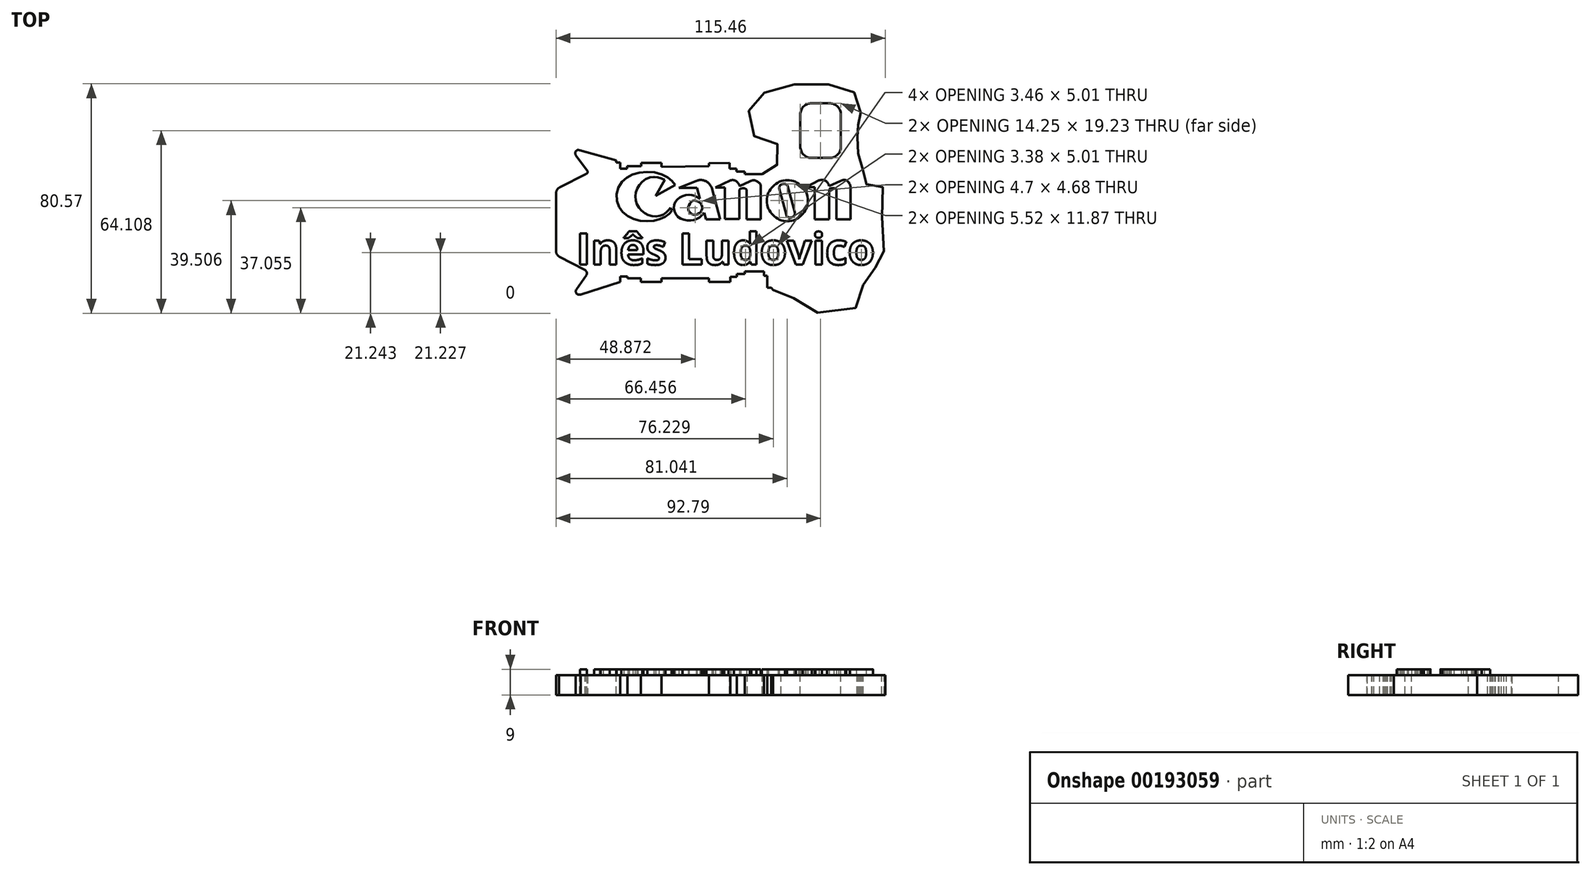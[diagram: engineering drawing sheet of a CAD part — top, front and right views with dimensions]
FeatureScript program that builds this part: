
annotation { "Feature Type Name" : "Feature", "Feature Type Description" : "" }
export const myFeature = defineFeature(function(context is Context, id is Id, definition is map)
    precondition{}
    {
        {
            var Q0;
            Q0=qCreatedBy(makeId("Top.planeOp"),FACE);
            var sketch = newSketch(context, id + "F0", { "sketchPlane" : qUnion([Q0])});
            skLineSegment(sketch, "E0", {"start": v(25.55, 22.7) * mm, "end": v(22.34, 17.11) * mm});
            skLineSegment(sketch, "E1", {"start": v(22.34, 17.11) * mm, "end": v(29.25, 20.87) * mm});
            skLineSegment(sketch, "E2", {"start": v(27.55, 12.91) * mm, "end": v(28.1, 11.89) * mm});
            skLineSegment(sketch, "E3", {"start": v(36.86, 19.9) * mm, "end": v(30.53, 19.9) * mm});
            skLineSegment(sketch, "E4", {"start": v(30.53, 19.9) * mm, "end": v(36.65, 22.37) * mm});
            skLineSegment(sketch, "E5", {"start": v(36.86, 19.9) * mm, "end": v(37.86, 16.15) * mm});
            skLineSegment(sketch, "E6", {"start": v(39.39, 11.08) * mm, "end": v(39.97, 8.89) * mm});
            skLineSegment(sketch, "E7", {"start": v(39.97, 8.89) * mm, "end": v(44.97, 8.89) * mm});
            skLineSegment(sketch, "E8", {"start": v(44.97, 8.89) * mm, "end": v(42.04, 19.9) * mm});
            skLineSegment(sketch, "E9", {"start": v(48.66, 22.57) * mm, "end": v(43.34, 20.06) * mm});
            skLineSegment(sketch, "E10", {"start": v(43.34, 20.06) * mm, "end": v(46.62, 20.06) * mm});
            skLineSegment(sketch, "E11", {"start": v(46.62, 20.06) * mm, "end": v(46.62, 8.93) * mm});
            skLineSegment(sketch, "E12", {"start": v(46.62, 8.93) * mm, "end": v(51.76, 8.93) * mm});
            skLineSegment(sketch, "E13", {"start": v(51.76, 8.93) * mm, "end": v(51.76, 19.12) * mm});
            skLineSegment(sketch, "E14", {"start": v(54.28, 19.05) * mm, "end": v(54.28, 8.84) * mm});
            skLineSegment(sketch, "E15", {"start": v(54.28, 8.84) * mm, "end": v(59.22, 8.84) * mm});
            skLineSegment(sketch, "E16", {"start": v(59.22, 8.84) * mm, "end": v(59.22, 20.47) * mm});
            skLineSegment(sketch, "E17", {"start": v(51.83, 20.55) * mm, "end": v(55.42, 22.2) * mm});
            skCircle(sketch, "E18", {"center": v(68.54, 15.4) * mm, "radius": 7.18 * mm});
            skLineSegment(sketch, "E19", {"start": v(65.68, 19.69) * mm, "end": v(68.18, 10.33) * mm});
            skLineSegment(sketch, "E20", {"start": v(68.64, 20.6) * mm, "end": v(71.14, 11.46) * mm});
            skLineSegment(sketch, "E21", {"start": v(79.7, 22.51) * mm, "end": v(75.06, 20.1) * mm});
            skLineSegment(sketch, "E22", {"start": v(75.06, 20.1) * mm, "end": v(78.1, 20.1) * mm});
            skLineSegment(sketch, "E23", {"start": v(78.1, 20.1) * mm, "end": v(78.1, 8.88) * mm});
            skLineSegment(sketch, "E24", {"start": v(78.1, 8.88) * mm, "end": v(83.2, 8.88) * mm});
            skLineSegment(sketch, "E25", {"start": v(83.2, 8.88) * mm, "end": v(83.2, 19.16) * mm});
            skLineSegment(sketch, "E26", {"start": v(85.75, 19) * mm, "end": v(85.75, 8.9) * mm});
            skLineSegment(sketch, "E27", {"start": v(85.75, 8.9) * mm, "end": v(90.69, 8.9) * mm});
            skLineSegment(sketch, "E28", {"start": v(90.69, 8.9) * mm, "end": v(90.69, 20.51) * mm});
            skLineSegment(sketch, "E29", {"start": v(83.21, 20.55) * mm, "end": v(87.16, 22.36) * mm});
            skFitSpline(sketch, "E30", {"points": [v(87.16, 22.36) * mm, v(88.44, 22.69) * mm, v(89.84, 22.08) * mm, v(90.69, 20.51) * mm], "startDerivative": vector(4.02, 1.64) * mm, "endDerivative": vector(1.85, -4.85) * mm});
            skFitSpline(sketch, "E31", {"points": [v(79.7, 22.51) * mm, v(80.8, 22.69) * mm, v(82.34, 22.06) * mm, v(83.21, 20.55) * mm], "startDerivative": vector(3.56, 1.05) * mm, "endDerivative": vector(1.86, -4.65) * mm});
            skFitSpline(sketch, "E32", {"points": [v(83.2, 19.16) * mm, v(84, 19.77) * mm, v(85.05, 19.78) * mm, v(85.75, 19) * mm], "startDerivative": vector(1.8, 4.83) * mm, "endDerivative": vector(0.96, -4.57) * mm});
            skFitSpline(sketch, "E33", {"points": [v(65.68, 19.69) * mm, v(66, 20.79) * mm, v(67.73, 21.3) * mm, v(68.64, 20.6) * mm], "startDerivative": vector(0.1, 3.88) * mm, "endDerivative": vector(2.36, -3) * mm});
            skFitSpline(sketch, "E34", {"points": [v(71.14, 11.46) * mm, v(70.7, 9.89) * mm, v(69.36, 9.46) * mm, v(68.18, 10.33) * mm], "startDerivative": vector(1.8, -7.45) * mm, "endDerivative": vector(-2.16, 5.47) * mm});
            skFitSpline(sketch, "E35", {"points": [v(55.42, 22.2) * mm, v(56.74, 22.57) * mm, v(58.26, 21.97) * mm, v(59.22, 20.47) * mm], "startDerivative": vector(4.12, 1.85) * mm, "endDerivative": vector(0.6, -6.79) * mm});
            skFitSpline(sketch, "E36", {"points": [v(51.76, 19.12) * mm, v(52.53, 19.72) * mm, v(53.4, 19.74) * mm, v(54.28, 19.05) * mm], "startDerivative": vector(0.57, 3.43) * mm, "endDerivative": vector(1.8, -4.71) * mm});
            skFitSpline(sketch, "E37", {"points": [v(48.66, 22.57) * mm, v(49.98, 22.57) * mm, v(51.2, 21.7) * mm, v(51.83, 20.55) * mm], "startDerivative": vector(4.07, 0.59) * mm, "endDerivative": vector(1.6, -3.62) * mm});
            skFitSpline(sketch, "E38", {"points": [v(36.65, 22.37) * mm, v(38.17, 22.68) * mm, v(39.66, 22.37) * mm, v(41.07, 21.46) * mm, v(42.04, 19.9) * mm], "startDerivative": vector(6.26, 1.9) * mm, "endDerivative": vector(3.2, -6.44) * mm});
            skFitSpline(sketch, "E39", {"points": [v(37.86, 16.15) * mm, v(35.45, 17.27) * mm, v(32.42, 17.24) * mm, v(29.68, 15.5) * mm, v(28.77, 12.57) * mm, v(30.3, 9.6) * mm, v(33.67, 8.48) * mm, v(36.81, 8.95) * mm, v(39.39, 11.08) * mm], "startDerivative": vector(-20.05, 11.67) * mm, "endDerivative": vector(18.93, 19.47) * mm});
            skFitSpline(sketch, "E40", {"points": [v(35.36, 15.28) * mm, v(34.05, 13.9) * mm, v(33.97, 11.85) * mm, v(35.58, 10.54) * mm, v(37.73, 11.06) * mm, v(38.7, 12.83) * mm, v(38.02, 14.6) * mm, v(36.69, 15.3) * mm, v(35.36, 15.28) * mm]});
            skFitSpline(sketch, "E41", {"points": [v(25.55, 22.7) * mm, v(22.92, 23.67) * mm, v(19.35, 23.24) * mm, v(16.4, 20.56) * mm, v(15.28, 17.49) * mm, v(15.73, 14.19) * mm, v(17.82, 11.56) * mm, v(20.57, 10.14) * mm, v(23.96, 10.1) * mm, v(26.14, 11.31) * mm, v(27.55, 12.91) * mm], "startDerivative": vector(-26.12, 12.48) * mm, "endDerivative": vector(15.76, 20.13) * mm});
            skFitSpline(sketch, "E42", {"points": [v(29.25, 20.87) * mm, v(27.38, 22.95) * mm, v(23.88, 24.86) * mm, v(18.1, 25.5) * mm, v(13.3, 24.13) * mm, v(10.2, 21.61) * mm, v(8.67, 17.42) * mm, v(9.54, 13.21) * mm, v(12.16, 10.3) * mm, v(16.04, 8.58) * mm, v(20.51, 8.24) * mm, v(24.56, 9.21) * mm, v(26.81, 10.52) * mm, v(28.1, 11.89) * mm], "startDerivative": vector(-25.89, 32.96) * mm, "endDerivative": vector(22.29, 26.43) * mm});
            skSolve(sketch);
        }
        {
            var Q0;
            Q0=makeQuery(id+"F0.imprint","IMPRINT",FACE,{"disambiguationData":[TD([[makeQuery(id+"F0.imprint","IMPRINT",EDGE,{"derivedFrom":sQuery(id+"F0.wireOp",EDGE,"E21")}),1.0]])]});
            var Q1;
            Q1=makeQuery(id+"F0.imprint","IMPRINT",FACE,{"disambiguationData":[TD([[makeQuery(id+"F0.imprint","IMPRINT",EDGE,{"derivedFrom":sQuery(id+"F0.wireOp",EDGE,"E18")}),1.0]])]});
            var Q2;
            Q2=makeQuery(id+"F0.imprint","IMPRINT",FACE,{"disambiguationData":[TD([[makeQuery(id+"F0.imprint","IMPRINT",EDGE,{"derivedFrom":sQuery(id+"F0.wireOp",EDGE,"E9")}),1.0]])]});
            var Q3;
            Q3=makeQuery(id+"F0.imprint","IMPRINT",FACE,{"disambiguationData":[TD([[makeQuery(id+"F0.imprint","IMPRINT",EDGE,{"derivedFrom":sQuery(id+"F0.wireOp",EDGE,"E3")}),-1.0]])]});
            var Q4;
            Q4=makeQuery(id+"F0.imprint","IMPRINT",FACE,{"disambiguationData":[TD([[makeQuery(id+"F0.imprint","IMPRINT",EDGE,{"derivedFrom":sQuery(id+"F0.wireOp",EDGE,"E0")}),1.0]])]});
            extrude(context, id + "F1", {"entities" : qUnion([Q0, Q1, Q2, Q3, Q4]), "depth" : 2 * mm});
        }
        {
            var Q0;
            Q0=qCreatedBy(makeId("Top.planeOp"),FACE);
            var sketch = newSketch(context, id + "F2", { "sketchPlane" : qUnion([Q0])});
            skText(sketch, "E43", { "text": "Inês Ludovico", "fontName": "OpenSans-Bold.ttf"});
            const initialGuessF2  = {"E43": [-0.0055, -0.00706, 1, 0, 0.01106]};
            skSetInitialGuess(sketch, initialGuessF2);
            skSolve(sketch);
        }
        {
            var Q0;
            Q0=qSketchRegion(id+"F2",true);
            extrude(context, id + "F3", {"entities" : qUnion([Q0]), "depth" : 2 * mm});
        }
        {
            var Q0;
            Q0=qCreatedBy(makeId("Top.planeOp"),FACE);
            var sketch = newSketch(context, id + "F4", { "sketchPlane" : qUnion([Q0])});
            skLineSegment(sketch, "E44", {"start": v(-4.27, 33.12) * mm, "end": v(8.5, 29.54) * mm});
            skLineSegment(sketch, "E45", {"start": v(8.5, 29.54) * mm, "end": v(8.5, 28.85) * mm});
            skLineSegment(sketch, "E46", {"start": v(8.5, 28.85) * mm, "end": v(9.98, 28.85) * mm});
            skLineSegment(sketch, "E47", {"start": v(9.98, 28.85) * mm, "end": v(9.98, 26.64) * mm});
            skLineSegment(sketch, "E48", {"start": v(9.98, 26.64) * mm, "end": v(12.34, 26.64) * mm});
            skLineSegment(sketch, "E49", {"start": v(12.34, 26.64) * mm, "end": v(12.34, 27.52) * mm});
            skLineSegment(sketch, "E50", {"start": v(12.34, 27.52) * mm, "end": v(17.25, 27.52) * mm});
            skLineSegment(sketch, "E51", {"start": v(17.25, 27.52) * mm, "end": v(17.25, 28.65) * mm});
            skLineSegment(sketch, "E52", {"start": v(17.25, 28.65) * mm, "end": v(24.43, 28.65) * mm});
            skLineSegment(sketch, "E53", {"start": v(24.43, 28.65) * mm, "end": v(24.43, 27.32) * mm});
            skLineSegment(sketch, "E54", {"start": v(24.43, 27.32) * mm, "end": v(41.08, 27.52) * mm});
            skPoint(sketch, "E54.endSnap0", {"position": v(14.8, 27.52) * mm});
            skLineSegment(sketch, "E55", {"start": v(41.08, 27.52) * mm, "end": v(41.07, 28.58) * mm});
            skLineSegment(sketch, "E56", {"start": v(41.07, 28.58) * mm, "end": v(48.22, 28.66) * mm});
            skLineSegment(sketch, "E57", {"start": v(48.22, 28.66) * mm, "end": v(48.25, 26.59) * mm});
            skLineSegment(sketch, "E58", {"start": v(48.25, 26.59) * mm, "end": v(50.73, 26.62) * mm});
            skLineSegment(sketch, "E59", {"start": v(50.73, 26.62) * mm, "end": v(50.74, 25.63) * mm});
            skLineSegment(sketch, "E60", {"start": v(50.74, 25.63) * mm, "end": v(53.6, 25.67) * mm});
            skLineSegment(sketch, "E61", {"start": v(53.6, 25.67) * mm, "end": v(53.6, 24.68) * mm});
            skLineSegment(sketch, "E62", {"start": v(53.6, 24.68) * mm, "end": v(59.69, 24.75) * mm});
            skFitSpline(sketch, "E63", {"points": [v(59.69, 24.75) * mm, v(60.26, 25.63) * mm, v(61.5, 26.44) * mm, v(62.74, 26.5) * mm, v(64.36, 27.37) * mm, v(65.59, 29) * mm, v(66.18, 31.16) * mm, v(66.23, 33.61) * mm, v(64.95, 35.33) * mm, v(62.98, 35.97) * mm, v(60.03, 36.37) * mm, v(57.33, 37.74) * mm, v(55.6, 39.48) * mm, v(54.53, 42.7) * mm, v(54.86, 46.33) * mm, v(55.75, 48.71) * mm, v(57.24, 50.7) * mm, v(59.17, 52.42) * mm, v(62.3, 54.24) * mm, v(66.1, 55.5) * mm, v(70.88, 56.17) * mm, v(76.66, 56.43) * mm, v(81.08, 56.38) * mm, v(85.82, 55.8) * mm, v(88.74, 55.18) * mm, v(91.03, 54.2) * mm, v(93.06, 51.8) * mm, v(93.84, 48.78) * mm, v(94, 47.13) * mm, v(94.05, 46.53) * mm, v(94.4, 46) * mm, v(94.47, 45.25) * mm, v(94.34, 44.1) * mm, v(93.9, 43.61) * mm, v(93.6, 43.28) * mm, v(93.5, 42.65) * mm, v(93.38, 41.84) * mm, v(93.53, 41.35) * mm, v(93.98, 40.92) * mm, v(94.23, 39.46) * mm, v(93.8, 38.5) * mm, v(93.3, 37.98) * mm, v(93.02, 37.4) * mm, v(93.06, 35.8) * mm, v(93.1, 33.97) * mm, v(93.1, 32.7) * mm, v(93.1, 32.15) * mm, v(93.42, 31.82) * mm, v(93.75, 31.22) * mm, v(93.84, 30.06) * mm, v(94.53, 29.32) * mm, v(95.04, 27.79) * mm, v(95, 25.6) * mm, v(94.77, 24.75) * mm, v(94.81, 23.92) * mm, v(95.6, 23) * mm, v(96.13, 22.21) * mm, v(96.35, 21.07) * mm, v(96.91, 21.07) * mm, v(98.27, 21.07) * mm, v(99.67, 21.07) * mm, v(101.12, 20.77) * mm, v(102.43, 19.28) * mm, v(102.22, 15.3) * mm, v(101.8, 10.84) * mm, v(101.68, 5.8) * mm, v(102, 0) * mm, v(102.58, -3.28) * mm, v(102.84, -5.38) * mm, v(101.88, -7.4) * mm, v(99.78, -8.18) * mm, v(97.24, -8.27) * mm, v(96.2, -10.19) * mm, v(95.5, -12.83) * mm, v(94.8, -15.64) * mm, v(94.46, -18.3) * mm, v(94, -20.63) * mm, v(91.03, -23.04) * mm, v(83.93, -24.1) * mm, v(77.9, -23.72) * mm, v(73.63, -22.18) * mm, v(71.42, -19.97) * mm, v(70.31, -18.2) * mm, v(68.55, -16.58) * mm, v(65.38, -15.92) * mm, v(63.47, -15.92) * mm], "startDerivative": vector(54.76, 104.15) * mm, "endDerivative": vector(-153.88, -5.36) * mm});
            skLineSegment(sketch, "E64", {"start": v(63.47, -15.92) * mm, "end": v(62.9, -15.16) * mm});
            skLineSegment(sketch, "E65", {"start": v(62.9, -15.16) * mm, "end": v(61.49, -15.16) * mm});
            skLineSegment(sketch, "E66", {"start": v(61.49, -15.16) * mm, "end": v(61.49, -11) * mm});
            skLineSegment(sketch, "E67", {"start": v(61.49, -11) * mm, "end": v(60.4, -11) * mm});
            skLineSegment(sketch, "E68", {"start": v(60.4, -11) * mm, "end": v(60.4, -9.49) * mm});
            skLineSegment(sketch, "E69", {"start": v(60.4, -9.49) * mm, "end": v(53.68, -9.49) * mm});
            skLineSegment(sketch, "E70", {"start": v(53.68, -9.49) * mm, "end": v(53.68, -10.27) * mm});
            skLineSegment(sketch, "E71", {"start": v(53.68, -10.27) * mm, "end": v(50.81, -10.27) * mm});
            skLineSegment(sketch, "E72", {"start": v(50.81, -10.27) * mm, "end": v(50.81, -11.3) * mm});
            skLineSegment(sketch, "E73", {"start": v(50.81, -11.3) * mm, "end": v(48.58, -11.3) * mm});
            skLineSegment(sketch, "E74", {"start": v(48.58, -11.3) * mm, "end": v(48.58, -13.08) * mm});
            skLineSegment(sketch, "E75", {"start": v(48.58, -13.08) * mm, "end": v(41.03, -13.08) * mm});
            skLineSegment(sketch, "E76", {"start": v(41.03, -13.08) * mm, "end": v(41.03, -11.83) * mm});
            skLineSegment(sketch, "E77", {"start": v(41.03, -11.83) * mm, "end": v(24.46, -11.83) * mm});
            skLineSegment(sketch, "E78", {"start": v(24.46, -11.83) * mm, "end": v(24.46, -13.08) * mm});
            skLineSegment(sketch, "E79", {"start": v(24.46, -13.08) * mm, "end": v(17.18, -13.08) * mm});
            skLineSegment(sketch, "E80", {"start": v(17.18, -13.08) * mm, "end": v(17.18, -11.83) * mm});
            skLineSegment(sketch, "E81", {"start": v(17.18, -11.83) * mm, "end": v(12.49, -11.83) * mm});
            skLineSegment(sketch, "E82", {"start": v(12.49, -11.83) * mm, "end": v(12.49, -11.25) * mm});
            skLineSegment(sketch, "E83", {"start": v(12.49, -11.25) * mm, "end": v(9.98, -11.25) * mm});
            skLineSegment(sketch, "E84", {"start": v(9.98, -11.25) * mm, "end": v(9.98, -13.08) * mm});
            skLineSegment(sketch, "E85", {"start": v(9.98, -13.08) * mm, "end": v(-3.92, -17.55) * mm});
            skLineSegment(sketch, "E86", {"start": v(-5.45, -15.73) * mm, "end": v(-1.92, -10.72) * mm});
            skLineSegment(sketch, "E87", {"start": v(-2.35, -8.98) * mm, "end": v(-11.49, -4.22) * mm});
            skLineSegment(sketch, "E88", {"start": v(-12.6, 17.98) * mm, "end": v(-12.6, -1.95) * mm});
            skLineSegment(sketch, "E89", {"start": v(-11.1, 20.15) * mm, "end": v(-2.07, 24.7) * mm});
            skLineSegment(sketch, "E90", {"start": v(-1.76, 26.16) * mm, "end": v(-5.65, 31.3) * mm});
            skFitSpline(sketch, "E91", {"points": [v(-4.27, 33.12) * mm, v(-5.17, 33.12) * mm, v(-5.86, 32.2) * mm, v(-5.65, 31.3) * mm], "startDerivative": vector(-2.87, 0.62) * mm, "endDerivative": vector(1.24, -2.69) * mm});
            skFitSpline(sketch, "E92", {"points": [v(-1.76, 26.16) * mm, v(-1.48, 25.5) * mm, v(-1.76, 24.95) * mm, v(-2.07, 24.7) * mm], "startDerivative": vector(1.15, -1.76) * mm, "endDerivative": vector(-1.11, -0.71) * mm});
            skFitSpline(sketch, "E93", {"points": [v(-11.1, 20.15) * mm, v(-11.86, 19.67) * mm, v(-12.42, 18.78) * mm, v(-12.6, 17.98) * mm], "startDerivative": vector(-2.4, -1.2) * mm, "endDerivative": vector(-0.4, -2.47) * mm});
            skFitSpline(sketch, "E94", {"points": [v(-11.49, -4.22) * mm, v(-12.1, -3.64) * mm, v(-12.48, -2.9) * mm, v(-12.6, -1.95) * mm], "startDerivative": vector(-2.05, 1.65) * mm, "endDerivative": vector(-0.19, 2.8) * mm});
            skFitSpline(sketch, "E95", {"points": [v(-2.35, -8.98) * mm, v(-1.93, -9.4) * mm, v(-1.76, -10.15) * mm, v(-1.92, -10.72) * mm], "startDerivative": vector(1.44, -1.13) * mm, "endDerivative": vector(-0.68, -1.68) * mm});
            skFitSpline(sketch, "E96", {"points": [v(-5.45, -15.73) * mm, v(-5.65, -16.45) * mm, v(-5.12, -17.41) * mm, v(-3.92, -17.55) * mm], "startDerivative": vector(-1.13, -2.3) * mm, "endDerivative": vector(3.62, 0.3) * mm});
            skLineSegment(sketch, "E97.bottom", {"start": v(77.07, 49.61) * mm, "end": v(83.32, 49.61) * mm});
            skLineSegment(sketch, "E97.top", {"start": v(77.07, 30.38) * mm, "end": v(83.32, 30.38) * mm});
            skLineSegment(sketch, "E97.left", {"start": v(73.07, 45.61) * mm, "end": v(73.07, 34.38) * mm});
            skLineSegment(sketch, "E97.right", {"start": v(87.32, 45.61) * mm, "end": v(87.32, 34.38) * mm});
            skPoint(sketch, "E98.visualSharp", {"position": v(73.07, 49.61) * mm});
            skArc(sketch, "E98.filletArc", {"start": v(77.07, 49.61) * mm, "mid": v(74.24, 48.44) * mm, "end": v(73.07, 45.61) * mm});
            skPoint(sketch, "E99.visualSharp", {"position": v(87.32, 49.61) * mm});
            skArc(sketch, "E99.filletArc", {"start": v(87.32, 45.61) * mm, "mid": v(86.14, 48.44) * mm, "end": v(83.32, 49.61) * mm});
            skPoint(sketch, "E100.visualSharp", {"position": v(73.07, 30.38) * mm});
            skArc(sketch, "E100.filletArc", {"start": v(73.07, 34.38) * mm, "mid": v(74.24, 31.55) * mm, "end": v(77.07, 30.38) * mm});
            skPoint(sketch, "E101.visualSharp", {"position": v(87.32, 30.38) * mm});
            skArc(sketch, "E101.filletArc", {"start": v(83.32, 30.38) * mm, "mid": v(86.14, 31.55) * mm, "end": v(87.32, 34.38) * mm});
            skPoint(sketch, "E102.center.orphan", {"position": v(84.14, -15.64) * mm});
            skPoint(sketch, "E103.end.orphan", {"position": v(86.67, -1.38) * mm});
            skPoint(sketch, "E104.5.internal.orphan", {"position": v(66.12, 0) * mm});
            skPoint(sketch, "E105.start.orphan", {"position": v(86.67, 17.03) * mm});
            skSolve(sketch);
        }
        {
            var Q0;
            Q0=makeQuery(id+"F4.imprint","IMPRINT",FACE,{"disambiguationData":[TD([[makeQuery(id+"F4.imprint","IMPRINT",EDGE,{"derivedFrom":sQuery(id+"F4.wireOp",EDGE,"E44")}),-1.0]])]});
            extrude(context, id + "F5", {"entities" : qUnion([Q0]), "oppositeDirection" : true, "depth" : 7 * mm});
        }
    });
